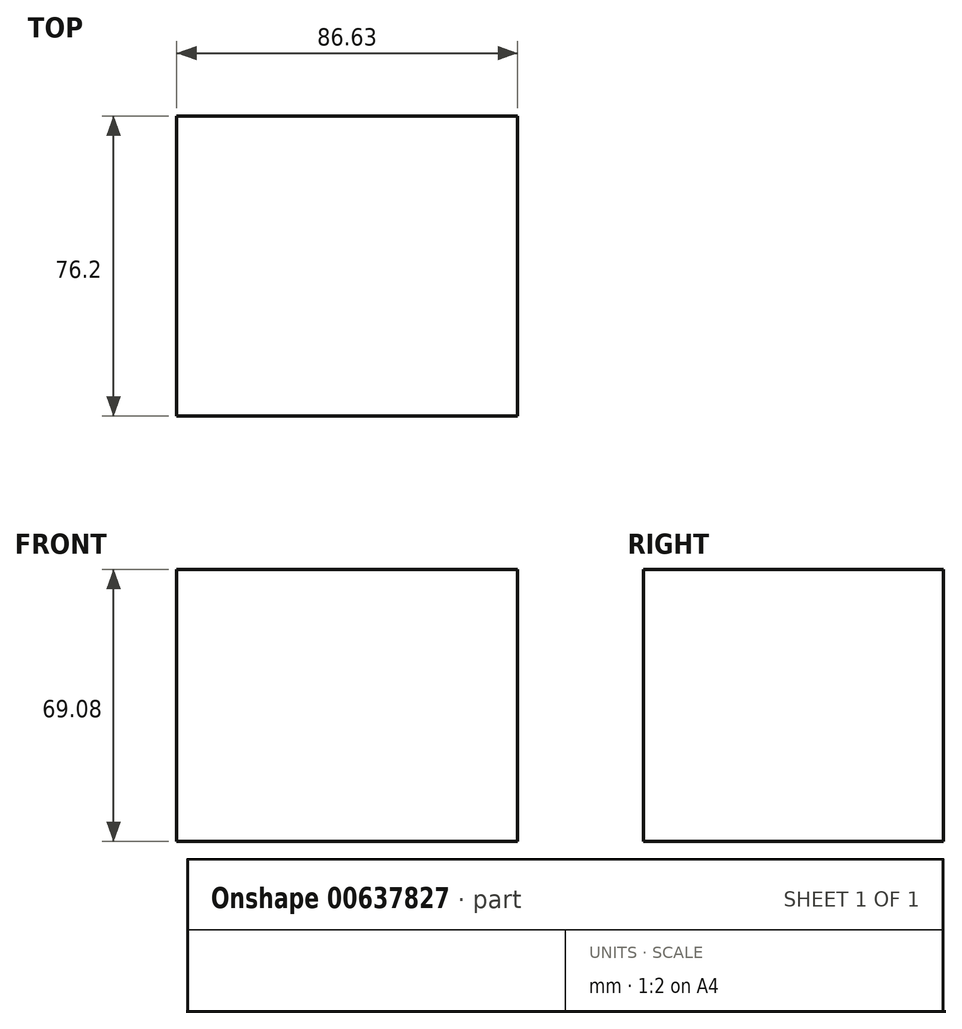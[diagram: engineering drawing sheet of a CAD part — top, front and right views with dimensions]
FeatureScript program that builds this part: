
annotation { "Feature Type Name" : "Feature", "Feature Type Description" : "" }
export const myFeature = defineFeature(function(context is Context, id is Id, definition is map)
    precondition{}
    {
        {
            var Q0;
            Q0=qCreatedBy(makeId("Front.planeOp"),FACE);
            var sketch = newSketch(context, id + "F0", { "sketchPlane" : qUnion([Q0])});
            skLineSegment(sketch, "E0.bottom", {"start": v(-42.74, 29.79) * mm, "end": v(43.9, 29.79) * mm});
            skLineSegment(sketch, "E0.top", {"start": v(-42.74, -39.29) * mm, "end": v(43.9, -39.29) * mm});
            skLineSegment(sketch, "E0.left", {"start": v(-42.74, 29.79) * mm, "end": v(-42.74, -39.29) * mm});
            skLineSegment(sketch, "E0.right", {"start": v(43.9, 29.79) * mm, "end": v(43.9, -39.29) * mm});
            skSolve(sketch);
        }
        {
            var Q0;
            Q0 = qSketchRegion(id + "F0", true);
            extrude(context, id + "F1", {"entities" : qUnion([Q0]), "depth" : 76.2 * mm, "offsetDistance" : 25.4 * mm});
        }
    });
